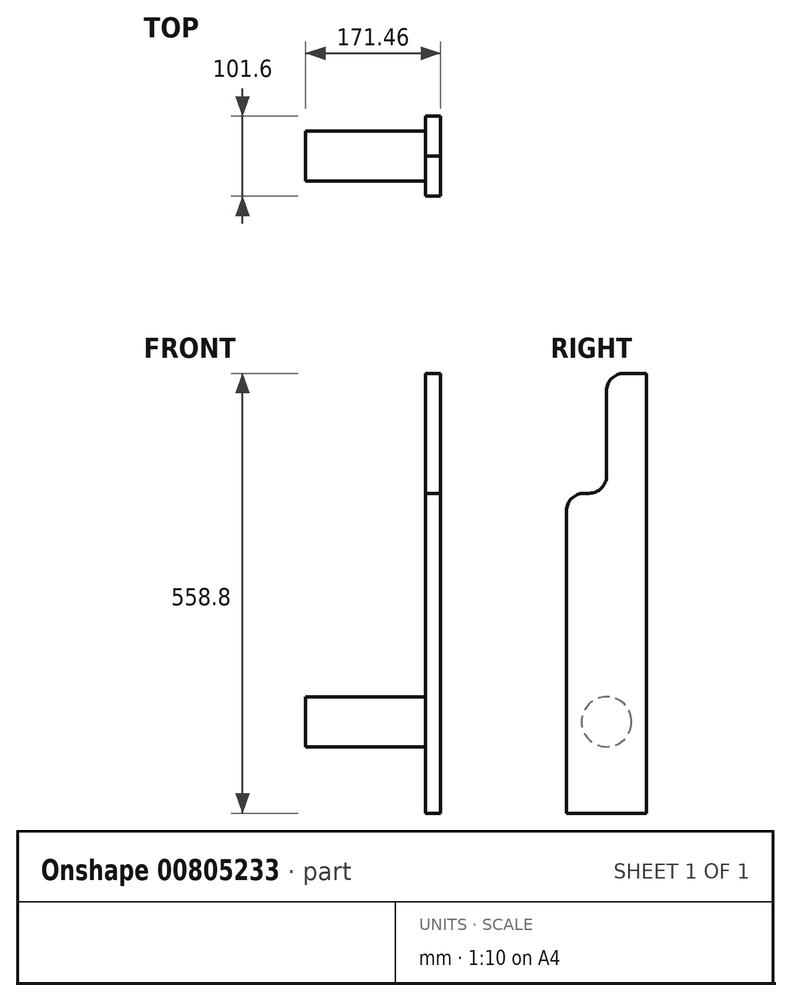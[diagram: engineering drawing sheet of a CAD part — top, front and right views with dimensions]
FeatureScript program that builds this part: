
annotation { "Feature Type Name" : "Feature", "Feature Type Description" : "" }
export const myFeature = defineFeature(function(context is Context, id is Id, definition is map)
    precondition{}
    {
        {
            var Q0;
            Q0=qCreatedBy(makeId("Right.planeOp"),FACE);
            var sketch = newSketch(context, id + "F0", { "sketchPlane" : qUnion([Q0])});
            skLineSegment(sketch, "E0", {"start": v(101.6, 355.6) * mm, "end": v(101.6, -203.2) * mm});
            skLineSegment(sketch, "E1", {"start": v(101.6, -203.2) * mm, "end": v(0, -203.2) * mm});
            skLineSegment(sketch, "E2", {"start": v(0, -203.2) * mm, "end": v(0, 203.2) * mm});
            skLineSegment(sketch, "E3", {"start": v(0, 203.2) * mm, "end": v(50.8, 203.2) * mm});
            skLineSegment(sketch, "E4", {"start": v(50.8, 203.2) * mm, "end": v(50.8, 355.6) * mm});
            skLineSegment(sketch, "E5", {"start": v(50.8, 355.6) * mm, "end": v(101.6, 355.6) * mm});
            skSolve(sketch);
        }
        {
            var Q0;
            Q0=qSketchRegion(id+"F0",true);
            extrude(context, id + "F1", {"entities" : qUnion([Q0]), "endBound" : BoundingType.SYMMETRIC, "depth" : 19.05 * mm, "offsetDistance" : 25.4 * mm});
        }
        {
            var Q0;
            Q0=makeQuery(id+"F1.opExtrude","SWEPT_EDGE",EDGE,{"disambiguationData":[OSD([sQuery(id+"F0.wireOp",EDGE,"E4"),sQuery(id+"F0.wireOp",EDGE,"E5")])]});
            var Q1;
            Q1=makeQuery(id+"F1.opExtrude","SWEPT_EDGE",EDGE,{"disambiguationData":[OSD([sQuery(id+"F0.wireOp",EDGE,"E3"),sQuery(id+"F0.wireOp",EDGE,"E4")])]});
            var Q2;
            Q2=makeQuery(id+"F1.opExtrude","SWEPT_EDGE",EDGE,{"disambiguationData":[OSD([sQuery(id+"F0.wireOp",EDGE,"E2"),sQuery(id+"F0.wireOp",EDGE,"E3")])]});
            fillet(context, id + "F2", {"entities" : qUnion([Q0, Q1, Q2]), "radius" : 22.22 * mm, "tangentPropagation" : true, "allowEdgeOverflow" : false});
        }
        {
            var Q0;
            Q0=makeQuery(id+"F1.opExtrude","CAP_FACE",FACE,{"disambiguationData":[OSD([sQuery(id+"F0.wireOp",EDGE,"E0"),sQuery(id+"F0.wireOp",EDGE,"E1"),sQuery(id+"F0.wireOp",EDGE,"E2"),sQuery(id+"F0.wireOp",EDGE,"E3"),sQuery(id+"F0.wireOp",EDGE,"E4"),sQuery(id+"F0.wireOp",EDGE,"E5")])],"isStart":true});
            var sketch = newSketch(context, id + "F3", { "sketchPlane" : qUnion([Q0])});
            skCircle(sketch, "E6", {"center": v(-50.8, -87.03) * mm, "radius": 31.75 * mm});
            skPoint(sketch, "E6.centerSnap0", {"position": v(-50.8, -203.2) * mm});
            skSolve(sketch);
        }
        {
            var Q0;
            Q0=makeQuery(id+"F3.imprint","IMPRINT",FACE,{"disambiguationData":[TD([[makeQuery(id+"F3.imprint","IMPRINT",EDGE,{"derivedFrom":sQuery(id+"F3.wireOp",EDGE,"E6")}),1.0]])]});
            extrude(context, id + "F4", {"entities" : qUnion([Q0]), "operationType" : NewBodyOperationType.ADD, "depth" : 152.4 * mm, "offsetDistance" : 25.4 * mm});
        }
    });
